# Revit family: FU_Stool_Sandler_Oswell 3-2PP
name_source: partatom
category: Furniture
units: mm (PartAtom-declared; Revit-internal decimal feet)

## family parameters
Always vertical = Yes
Cut with Voids When Loaded = No
OmniClass Number = 23.40.20.00
OmniClass Title = General Furniture and Specialties
Render Appearance Source = Family Geometry
Room Calculation Point = No
Shared = No
Work Plane-Based = No

## types (1)
- Oswell 3.2PP
    Default Elevation = 0 mm  [stored 0 ft]
    Depth = 570 mm  [stored 1.87008 ft]
    Description = Stacking barstool with steel legs. The ridged polypropylene seat features a non-slip texture. This Greenguard Gold-certified stool stacks up to 6 units high and is made from 43% recycled materials.
    Height = 1110 mm  [stored 3.64173 ft]
    Manufacturer = Sandler
    Model = Oswell 3.2PP
    URL = https://www.sandlerseating.com
    Width = 515 mm  [stored 1.68963 ft]

note: [stored X ft] marks values corroborated as IEEE doubles in the binary element streams (Revit-internal decimal feet)

## geometry (parser evidence)
native form markers: Sweep x5
no freeform markers — native parametric forms only
